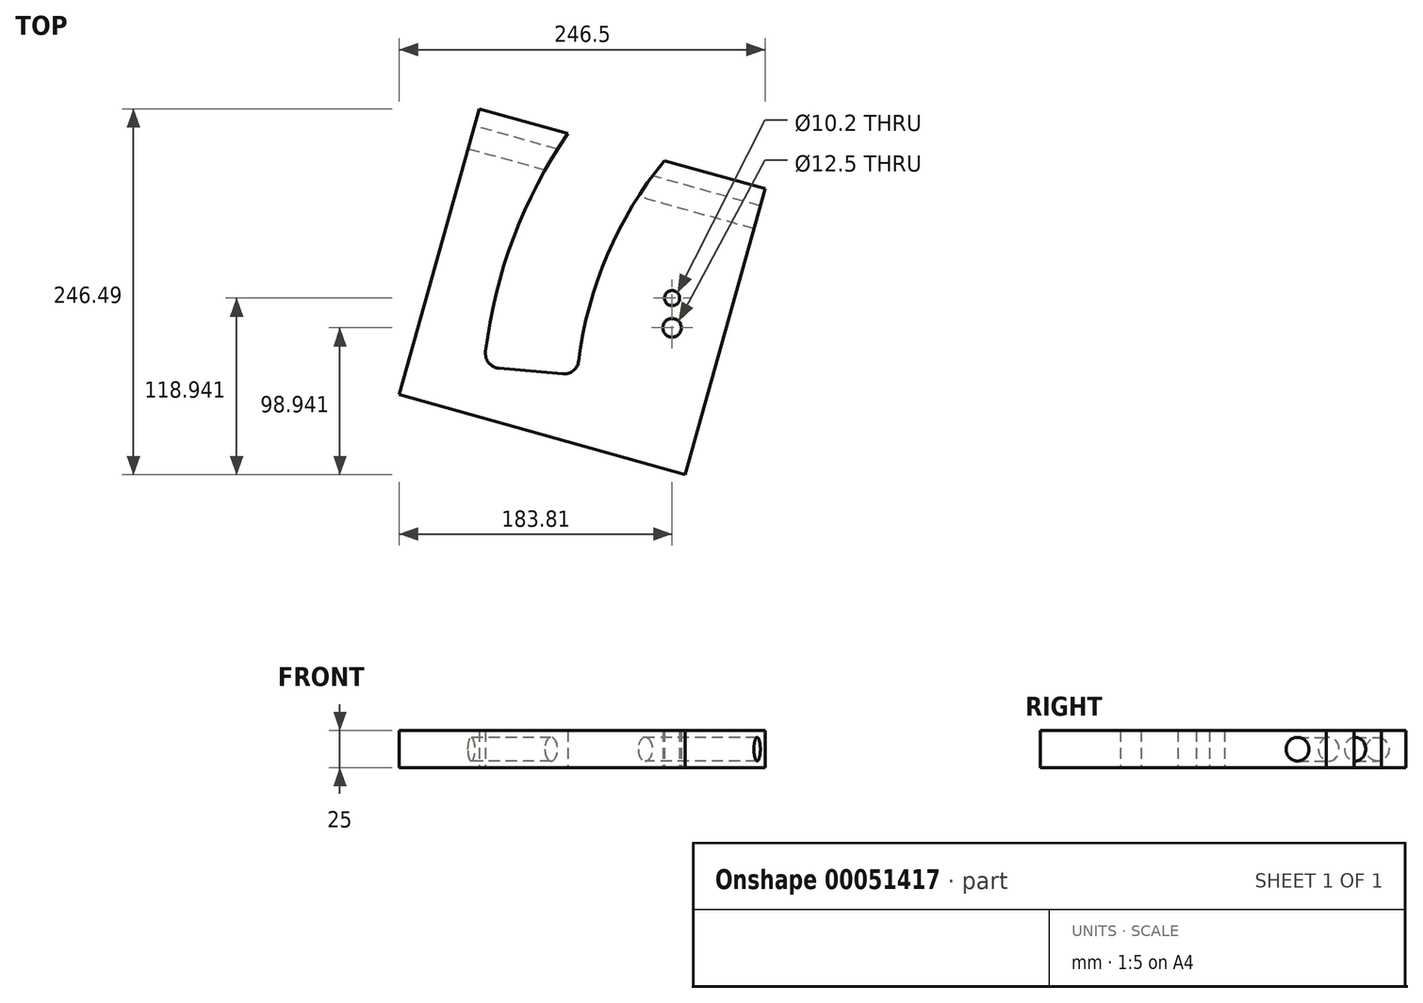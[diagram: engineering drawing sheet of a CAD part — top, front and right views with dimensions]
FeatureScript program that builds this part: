
annotation { "Feature Type Name" : "Feature", "Feature Type Description" : "" }
export const myFeature = defineFeature(function(context is Context, id is Id, definition is map)
    precondition{}
    {
        {
            var Q0;
            Q0=qCreatedBy(makeId("Top.planeOp"),FACE);
            var sketch = newSketch(context, id + "F0", { "sketchPlane" : qUnion([Q0])});
            skLineSegment(sketch, "E0", {"start": v(203.34, -80.72) * mm, "end": v(203.34, 279.82) * mm, "construction": true});
            skLineSegment(sketch, "E1", {"start": v(203.34, -80.72) * mm, "end": v(80.42, -69.96) * mm, "construction": true});
            skLineSegment(sketch, "E2.trimOffspring", {"start": v(-60.65, -57.62) * mm, "end": v(-123.41, -52.13) * mm});
            skCircle(sketch, "E3", {"center": v(3.34, -5.72) * mm, "radius": 5.1 * mm});
            skCircle(sketch, "E4", {"center": v(3.34, -25.72) * mm, "radius": 6.25 * mm});
            skArc(sketch, "E5.trimOffspring", {"start": v(-66.92, 105.14) * mm, "mid": v(-105.35, 30.16) * mm, "end": v(-123.41, -52.13) * mm});
            skArc(sketch, "E6.trimOffspring", {"start": v(-1.88, 86.94) * mm, "mid": v(-42.15, 19.08) * mm, "end": v(-60.65, -57.62) * mm});
            skLineSegment(sketch, "E7", {"start": v(203.34, -80.72) * mm, "end": v(-107.43, 2.55) * mm, "construction": true});
            skLineSegment(sketch, "E8", {"start": v(66.03, 67.94) * mm, "end": v(12.14, -124.66) * mm});
            skPoint(sketch, "E8.endSnap0", {"position": v(47.95, -39.08) * mm});
            skPoint(sketch, "E9.start.orphan", {"position": v(47.95, 3.35) * mm});
            skLineSegment(sketch, "E10", {"start": v(66.03, 67.94) * mm, "end": v(-1.88, 86.94) * mm});
            skLineSegment(sketch, "E11", {"start": v(12.14, -124.66) * mm, "end": v(-180.47, -70.77) * mm});
            skLineSegment(sketch, "E12", {"start": v(-126.57, 121.83) * mm, "end": v(-180.47, -70.77) * mm});
            skLineSegment(sketch, "E13.trimOffspring", {"start": v(-66.92, 105.14) * mm, "end": v(-126.57, 121.83) * mm});
            skSolve(sketch);
        }
        {
            var Q0;
            Q0 = qSketchRegion(id + "Fu6gjdzGZH9kaLb_112", true);
            var Q1;
            Q1=makeQuery(id+"F0.imprint","IMPRINT",FACE,{"disambiguationData":[TD([[makeQuery(id+"F0.imprint","IMPRINT",EDGE,{"derivedFrom":sQuery(id+"F0.wireOp",EDGE,"E2.trimOffspring")}),1.0]])]});
            extrude(context, id + "F1", {"entities" : qUnion([Q0, Q1]), "depth" : 25 * mm});
        }
        {
            var Q0;
            Q0=makeQuery(id+"F1.opExtrude","SWEPT_EDGE",EDGE,{"disambiguationData":[OSD([sQuery(id+"F0.wireOp",EDGE,"E2.trimOffspring"),sQuery(id+"F0.wireOp",EDGE,"E5.trimOffspring")])]});
            var Q1;
            Q1=makeQuery(id+"F1.opExtrude","SWEPT_EDGE",EDGE,{"disambiguationData":[OSD([sQuery(id+"F0.wireOp",EDGE,"E2.trimOffspring"),sQuery(id+"F0.wireOp",EDGE,"E6.trimOffspring")])]});
            fillet(context, id + "F2", {"entities" : qUnion([Q0, Q1]), "radius" : 10 * mm, "tangentPropagation" : true, "allowEdgeOverflow" : false});
        }
        {
            var Q0;
            Q0=makeQuery(id+"F1.opExtrude","SWEPT_FACE",FACE,{"disambiguationData":[OSD([sQuery(id+"F0.wireOp",EDGE,"E12")])]});
            var sketch = newSketch(context, id + "F3", { "sketchPlane" : qUnion([Q0])});
            skCircle(sketch, "E14", {"center": v(-63.22, 12.5) * mm, "radius": 8 * mm});
            skLineSegment(sketch, "E15", {"start": v(-83.22, 12.5) * mm, "end": v(116.78, 12.5) * mm, "construction": true});
            skSolve(sketch);
        }
        {
            var Q0;
            Q0 = qSketchRegion(id + "F3", true);
            var Q1;
            Q1=makeQuery(id+"F1.opExtrude","SWEPT_FACE",FACE,{"disambiguationData":[OSD([sQuery(id+"F0.wireOp",EDGE,"E8")])]});
            extrude(context, id + "F4", {"entities" : qUnion([Q0]), "operationType" : NewBodyOperationType.REMOVE, "endBound" : BoundingType.UP_TO_SURFACE, "oppositeDirection" : true, "endBoundEntityFace" : qUnion([Q1]), "depth" : 25 * mm});
        }
    });
